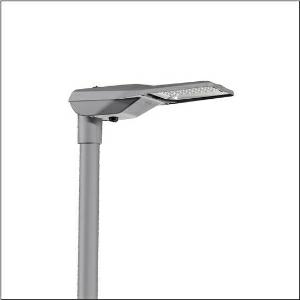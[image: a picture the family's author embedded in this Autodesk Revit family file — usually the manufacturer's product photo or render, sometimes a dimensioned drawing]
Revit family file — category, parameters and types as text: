
# Revit family: streetlight_sl_21_mini___st0_5a_5xe2b33t08hb_07ec
name_source: partatom
category: Lighting Fixtures
units: mm (PartAtom-declared; Revit-internal decimal feet)

## family parameters
Cut with Voids When Loaded = No
Host = Face
Light Source = No
Part Type = Normal
Room Calculation Point = No
Round Connector Dimension = Use Diameter
Shared = No

## types (1)
- --- (1 x LED, 9040 lm, 66 W, 3000K)
    Apparent Load = 66 VA
    CIE Flux Codes = 41 75 97 100 100
    Color Rendering = 70
    Color Temperature = 3000K
    Default Elevation = 1800 mm
    Description = Streetlight SL 21 mini, mast luminaire, primary light control with lens, of PMMA, primary optical cover: cover, of toughened safety glass, transparent, light distribution: ST0.5a, light emission: direct distribution, primary light characteristic: asymmetric, installation type: side-entry, post-top, LED, High Power LED, rated luminous flux: 9.040lm, luminous efficacy: 137lm/W, light colour: 730, colour temperature: 3000K, control gear: D4i, control: overheat protection, constant luminous flux control, time-dependent luminous flux control, flexible luminous flux parameterisation, pre-setting: logarithmic dimming characteristic, mains connection: 220..240V, AC, 50/60Hz, start of lifetime: 66W, end of service life: 69W, reduction: 30W, luminaire housing, of diecast aluminium, powder-coated, Siteco® metallic grey (DB 702S), corrosivity category C5 mid according to DIN EN ISO 12944, please order mast flange separately, inclination adjustable: 0°, 5°, 10°, 15°, sealing non-destructively replaceable, multi-level sealing system, length: 628mm, width: 235mm, height: 110mm, mast flange for spigot size: 42mm (side-entry): 5XC10008XM4, 60/48mm (side-entry/post-top): 5XC10108XM2, 76/60mm (side-entry/post-top): 5XC10108XM1, mounting height: 4..8m, Smart Interface below and above, protection rating (complete): IP66, insulation class (complete): insulation class II (safety insulation), certification: CE, ENEC, ENEC+, VDE, impact resistance: IK10, permissible operating ambient temperature for outdoor applications: -40..+50°C, standard-compliant lighting for roads and squares, packaging unit: 1 piece

Light Distribution: ST0.5a
    Height = 110 mm
    Lamp = 1 x LED
    Lamp Light Flux = 9040 lm
    Lamp Power = 66 W
    Lamp count = 1
    Length = 625 mm
    Luminous efficacy = 137 lm/W
    Manufacturer = Siteco
    ModVariant = No
    Model = 5XE2B33T08HB
    Number of Poles = 1
    OnlyDefault = Yes
    Power Factor = 1
    Product Name = Streetlight SL 21 mini | ST0.5a
    Product group = mast luminaire | pylon top
    ProductGroupID = 6100
    Protection Class = Protection class II
    Protection Degree = IP 66
    RLX_Detail_Level = 1
    RLX_Emergency_Light_Flux = 0 lm
    RLX_Emergency_Type = 0
    RLX_Emergency_Type_DB = No
    RlxData = <blob elided: 37257 chars, md5=6f29e66a>
    Socket = socket
    Standby Power = 0 W
    System Light Flux = 9040 lm
    System Power = 66 W
    Type Comments = factory setting: luminous flux: 100 % | dim-lin: 254 | 670 mA
    Type Image = l_1003514.jpg
    URL = http://relux.com
    VarID = @adj_212339
    Voltage = 0 V
    Weight = 0.00 kg
    Width = 234 mm

## geometry (parser evidence)
native form markers: Blend x4, Sweep x9
no freeform markers — native parametric forms only
